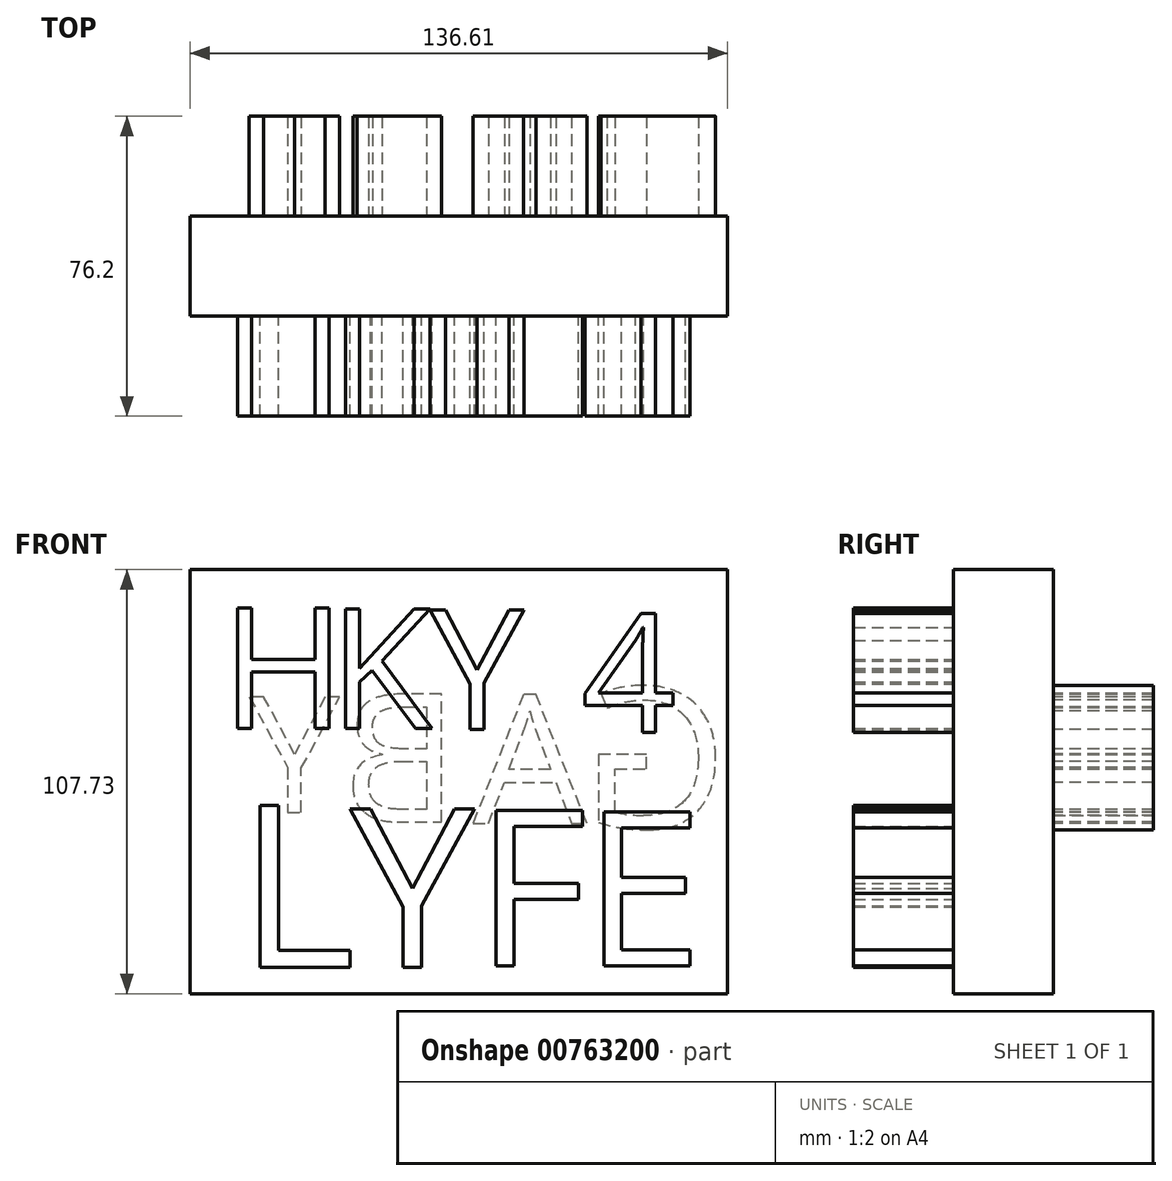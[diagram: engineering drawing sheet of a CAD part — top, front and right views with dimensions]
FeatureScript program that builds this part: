
annotation { "Feature Type Name" : "Feature", "Feature Type Description" : "" }
export const myFeature = defineFeature(function(context is Context, id is Id, definition is map)
    precondition{}
    {
        {
            var Q0;
            Q0=qCreatedBy(makeId("Front.planeOp"),FACE);
            var sketch = newSketch(context, id + "F0", { "sketchPlane" : qUnion([Q0])});
            skLineSegment(sketch, "E0.bottom", {"start": v(-70.77, 48.65) * mm, "end": v(65.84, 48.65) * mm});
            skLineSegment(sketch, "E0.top", {"start": v(-70.77, -59.08) * mm, "end": v(65.84, -59.08) * mm});
            skLineSegment(sketch, "E0.left", {"start": v(-70.77, 48.65) * mm, "end": v(-70.77, -59.08) * mm});
            skLineSegment(sketch, "E0.right", {"start": v(65.84, 48.65) * mm, "end": v(65.84, -59.08) * mm});
            skSolve(sketch);
        }
        {
            var Q0;
            Q0=makeQuery(id+"F0.imprint","IMPRINT",FACE,{"disambiguationData":[TD([[makeQuery(id+"F0.imprint","IMPRINT",EDGE,{"derivedFrom":sQuery(id+"F0.wireOp",EDGE,"E0.bottom")}),-1.0]])]});
            extrude(context, id + "F1", {"entities" : qUnion([Q0]), "depth" : 25.4 * mm, "offsetDistance" : 25.4 * mm});
        }
        {
            var Q0;
            Q0=makeQuery(id+"F1.opExtrude","CAP_FACE",FACE,{"disambiguationData":[OSD([sQuery(id+"F0.wireOp",EDGE,"E0.bottom"),sQuery(id+"F0.wireOp",EDGE,"E0.top"),sQuery(id+"F0.wireOp",EDGE,"E0.left"),sQuery(id+"F0.wireOp",EDGE,"E0.right")])],"isStart":false});
            var sketch = newSketch(context, id + "F2", { "sketchPlane" : qUnion([Q0])});
            skText(sketch, "E1", { "text": "H", "fontName": "OpenSans-Regular.ttf"});
            const initialGuessF2  = {"E1": [-0.06285, 0.00825, 1, 0, 0.0309]};
            skSetInitialGuess(sketch, initialGuessF2);
            skSolve(sketch);
        }
        {
            var Q0;
            Q0=makeQuery(id+"F2.imprint","IMPRINT",FACE,{"disambiguationData":[TD([[makeQuery(id+"F2.imprint","IMPRINT",EDGE,{"derivedFrom":sQuery(id+"F2.wireOp",EDGE,"E1.sketch_text.stroke-0")}),-1.0]])]});
            extrude(context, id + "F3", {"entities" : qUnion([Q0]), "operationType" : NewBodyOperationType.ADD, "depth" : 25.4 * mm, "offsetDistance" : 25.4 * mm});
        }
        {
            var Q0;
            Q0=makeQuery(id+"F1.opExtrude","CAP_FACE",FACE,{"disambiguationData":[OSD([sQuery(id+"F0.wireOp",EDGE,"E0.bottom"),sQuery(id+"F0.wireOp",EDGE,"E0.top"),sQuery(id+"F0.wireOp",EDGE,"E0.left"),sQuery(id+"F0.wireOp",EDGE,"E0.right")])],"isStart":false});
            var sketch = newSketch(context, id + "F4", { "sketchPlane" : qUnion([Q0])});
            skText(sketch, "E2", { "text": "K", "fontName": "OpenSans-Regular.ttf"});
            const initialGuessF4  = {"E2": [-0.03537, 0.00825, 1, 0, 0.03064]};
            skSetInitialGuess(sketch, initialGuessF4);
            skSolve(sketch);
        }
        {
            var Q0;
            Q0 = qSketchRegion(id + "F4", true);
            extrude(context, id + "F5", {"entities" : qUnion([Q0]), "operationType" : NewBodyOperationType.ADD, "depth" : 25.4 * mm, "offsetDistance" : 25.4 * mm});
        }
        {
            var Q0;
            Q0=makeQuery(id+"F1.opExtrude","CAP_FACE",FACE,{"disambiguationData":[OSD([sQuery(id+"F0.wireOp",EDGE,"E0.bottom"),sQuery(id+"F0.wireOp",EDGE,"E0.top"),sQuery(id+"F0.wireOp",EDGE,"E0.left"),sQuery(id+"F0.wireOp",EDGE,"E0.right")])],"isStart":false});
            var sketch = newSketch(context, id + "F6", { "sketchPlane" : qUnion([Q0])});
            skText(sketch, "E3", { "text": "Y", "fontName": "OpenSans-Regular.ttf"});
            const initialGuessF6  = {"E3": [-0.00971, 0.00806, 1, 0, 0.03057]};
            skSetInitialGuess(sketch, initialGuessF6);
            skSolve(sketch);
        }
        {
            var Q0;
            Q0 = qSketchRegion(id + "F6", true);
            extrude(context, id + "F7", {"entities" : qUnion([Q0]), "operationType" : NewBodyOperationType.ADD, "depth" : 25.4 * mm, "offsetDistance" : 25.4 * mm});
        }
        {
            var Q0;
            Q0=makeQuery(id+"F1.opExtrude","CAP_FACE",FACE,{"disambiguationData":[OSD([sQuery(id+"F0.wireOp",EDGE,"E0.bottom"),sQuery(id+"F0.wireOp",EDGE,"E0.top"),sQuery(id+"F0.wireOp",EDGE,"E0.left"),sQuery(id+"F0.wireOp",EDGE,"E0.right")])],"isStart":false});
            var sketch = newSketch(context, id + "F8", { "sketchPlane" : qUnion([Q0])});
            skText(sketch, "E4", { "text": "4", "fontName": "OpenSans-Regular.ttf"});
            const initialGuessF8  = {"E4": [0.02872, 0.0073, 1, 0, 0.03034]};
            skSetInitialGuess(sketch, initialGuessF8);
            skSolve(sketch);
        }
        {
            var Q0;
            Q0=makeQuery(id+"F8.imprint","IMPRINT",FACE,{"disambiguationData":[TD([[makeQuery(id+"F8.imprint","IMPRINT",EDGE,{"derivedFrom":sQuery(id+"F8.wireOp",EDGE,"E4.sketch_text.stroke-0")}),-1.0]])]});
            extrude(context, id + "F9", {"entities" : qUnion([Q0]), "operationType" : NewBodyOperationType.ADD, "depth" : 25.4 * mm, "offsetDistance" : 25.4 * mm});
        }
        {
            var Q0;
            {var subQ0=sQuery(id+"F0.wireOp",EDGE,"E0.top");var subQ1=sQuery(id+"F0.wireOp",EDGE,"E0.bottom");var subQ2=sQuery(id+"F0.wireOp",EDGE,"E0.left");var subQ3=sQuery(id+"F0.wireOp",EDGE,"E0.right");Q0=makeQuery(id+"F9.boolean.opBoolean","SPLIT",FACE,{"disambiguationData":[TD([makeQuery(id+"F1.opExtrude","SWEPT_FACE",FACE,{"disambiguationData":[OSD([subQ1])]})])],"derivedFrom":makeQuery(id+"F1.opExtrude","CAP_FACE",FACE,{"disambiguationData":[OSD([subQ1,subQ0,subQ2,subQ3])],"isStart":false})});}
            var sketch = newSketch(context, id + "F10", { "sketchPlane" : qUnion([Q0])});
            skText(sketch, "E5", { "text": "L", "fontName": "OpenSans-Regular.ttf"});
            const initialGuessF10  = {"E5": [-0.05864, -0.05242, 1, 0, 0.04152]};
            skSetInitialGuess(sketch, initialGuessF10);
            skSolve(sketch);
        }
        {
            var Q0;
            Q0 = qSketchRegion(id + "F10", true);
            extrude(context, id + "F11", {"entities" : qUnion([Q0]), "operationType" : NewBodyOperationType.ADD, "depth" : 25.4 * mm, "offsetDistance" : 25.4 * mm});
        }
        {
            var Q0;
            {var subQ0=sQuery(id+"F0.wireOp",EDGE,"E0.top");var subQ1=sQuery(id+"F0.wireOp",EDGE,"E0.bottom");var subQ2=sQuery(id+"F0.wireOp",EDGE,"E0.left");var subQ3=sQuery(id+"F0.wireOp",EDGE,"E0.right");Q0=makeQuery(id+"F9.boolean.opBoolean","SPLIT",FACE,{"disambiguationData":[TD([makeQuery(id+"F1.opExtrude","SWEPT_FACE",FACE,{"disambiguationData":[OSD([subQ1])]})])],"derivedFrom":makeQuery(id+"F1.opExtrude","CAP_FACE",FACE,{"disambiguationData":[OSD([subQ1,subQ0,subQ2,subQ3])],"isStart":false})});}
            var sketch = newSketch(context, id + "F12", { "sketchPlane" : qUnion([Q0])});
            skText(sketch, "E6", { "text": "Y", "fontName": "OpenSans-Regular.ttf"});
            const initialGuessF12  = {"E6": [-0.03003, -0.05242, 1, 0, 0.04057]};
            skSetInitialGuess(sketch, initialGuessF12);
            skSolve(sketch);
        }
        {
            var Q0;
            Q0=makeQuery(id+"F12.imprint","IMPRINT",FACE,{"disambiguationData":[TD([[makeQuery(id+"F12.imprint","IMPRINT",EDGE,{"derivedFrom":sQuery(id+"F12.wireOp",EDGE,"E6.sketch_text.stroke-0")}),-1.0]])]});
            extrude(context, id + "F13", {"entities" : qUnion([Q0]), "operationType" : NewBodyOperationType.ADD, "depth" : 25.4 * mm, "offsetDistance" : 25.4 * mm});
        }
        {
            var Q0;
            {var subQ0=sQuery(id+"F0.wireOp",EDGE,"E0.top");var subQ1=sQuery(id+"F0.wireOp",EDGE,"E0.bottom");var subQ2=sQuery(id+"F0.wireOp",EDGE,"E0.left");var subQ3=sQuery(id+"F0.wireOp",EDGE,"E0.right");Q0=makeQuery(id+"F9.boolean.opBoolean","SPLIT",FACE,{"disambiguationData":[TD([makeQuery(id+"F1.opExtrude","SWEPT_FACE",FACE,{"disambiguationData":[OSD([subQ1])]})])],"derivedFrom":makeQuery(id+"F1.opExtrude","CAP_FACE",FACE,{"disambiguationData":[OSD([subQ1,subQ0,subQ2,subQ3])],"isStart":false})});}
            var sketch = newSketch(context, id + "F14", { "sketchPlane" : qUnion([Q0])});
            skText(sketch, "E7", { "text": "F", "fontName": "OpenSans-Regular.ttf"});
            const initialGuessF14  = {"E7": [0.00153, -0.05204, 1, 0, 0.03985]};
            skSetInitialGuess(sketch, initialGuessF14);
            skSolve(sketch);
        }
        {
            var Q0;
            Q0=makeQuery(id+"F14.imprint","IMPRINT",FACE,{"disambiguationData":[TD([[makeQuery(id+"F14.imprint","IMPRINT",EDGE,{"derivedFrom":sQuery(id+"F14.wireOp",EDGE,"E7.sketch_text.stroke-0")}),-1.0]])]});
            extrude(context, id + "F15", {"entities" : qUnion([Q0]), "operationType" : NewBodyOperationType.ADD, "depth" : 25.4 * mm, "offsetDistance" : 25.4 * mm});
        }
        {
            var Q0;
            {var subQ0=sQuery(id+"F0.wireOp",EDGE,"E0.top");var subQ1=sQuery(id+"F0.wireOp",EDGE,"E0.bottom");var subQ2=sQuery(id+"F0.wireOp",EDGE,"E0.left");var subQ3=sQuery(id+"F0.wireOp",EDGE,"E0.right");Q0=makeQuery(id+"F9.boolean.opBoolean","SPLIT",FACE,{"disambiguationData":[TD([makeQuery(id+"F1.opExtrude","SWEPT_FACE",FACE,{"disambiguationData":[OSD([subQ1])]})])],"derivedFrom":makeQuery(id+"F1.opExtrude","CAP_FACE",FACE,{"disambiguationData":[OSD([subQ1,subQ0,subQ2,subQ3])],"isStart":false})});}
            var sketch = newSketch(context, id + "F16", { "sketchPlane" : qUnion([Q0])});
            skText(sketch, "E8", { "text": "E", "fontName": "OpenSans-Regular.ttf"});
            const initialGuessF16  = {"E8": [0.02899, -0.05204, 1, 0, 0.03951]};
            skSetInitialGuess(sketch, initialGuessF16);
            skSolve(sketch);
        }
        {
            var Q0;
            Q0=makeQuery(id+"F16.imprint","IMPRINT",FACE,{"disambiguationData":[TD([[makeQuery(id+"F16.imprint","IMPRINT",EDGE,{"derivedFrom":sQuery(id+"F16.wireOp",EDGE,"E8.sketch_text.stroke-0")}),-1.0]])]});
            extrude(context, id + "F17", {"entities" : qUnion([Q0]), "operationType" : NewBodyOperationType.ADD, "depth" : 25.4 * mm, "offsetDistance" : 25.4 * mm});
        }
        {
            var Q0;
            Q0=makeQuery(id+"F1.opExtrude","CAP_FACE",FACE,{"disambiguationData":[OSD([sQuery(id+"F0.wireOp",EDGE,"E0.bottom"),sQuery(id+"F0.wireOp",EDGE,"E0.top"),sQuery(id+"F0.wireOp",EDGE,"E0.left"),sQuery(id+"F0.wireOp",EDGE,"E0.right")])],"isStart":true});
            var sketch = newSketch(context, id + "F18", { "sketchPlane" : qUnion([Q0])});
            skText(sketch, "E9", { "text": "G", "fontName": "OpenSans-Regular.ttf"});
            const initialGuessF18  = {"E9": [-0.06584, -0.01696, 1, 0, 0.03601]};
            skSetInitialGuess(sketch, initialGuessF18);
            skSolve(sketch);
        }
        {
            var Q0;
            Q0=makeQuery(id+"F18.imprint","IMPRINT",FACE,{"disambiguationData":[TD([[makeQuery(id+"F18.imprint","IMPRINT",EDGE,{"derivedFrom":sQuery(id+"F18.wireOp",EDGE,"E9.sketch_text.stroke-0")}),-1.0]])]});
            extrude(context, id + "F19", {"entities" : qUnion([Q0]), "operationType" : NewBodyOperationType.ADD, "depth" : 25.4 * mm, "offsetDistance" : 25.4 * mm});
        }
        {
            var Q0;
            Q0=makeQuery(id+"F1.opExtrude","CAP_FACE",FACE,{"disambiguationData":[OSD([sQuery(id+"F0.wireOp",EDGE,"E0.bottom"),sQuery(id+"F0.wireOp",EDGE,"E0.top"),sQuery(id+"F0.wireOp",EDGE,"E0.left"),sQuery(id+"F0.wireOp",EDGE,"E0.right")])],"isStart":true});
            var sketch = newSketch(context, id + "F20", { "sketchPlane" : qUnion([Q0])});
            skText(sketch, "E10", { "text": "A", "fontName": "OpenSans-Regular.ttf"});
            const initialGuessF20  = {"E10": [-0.03005, -0.01583, 1, 0, 0.03288]};
            skSetInitialGuess(sketch, initialGuessF20);
            skSolve(sketch);
        }
        {
            var Q0;
            Q0=makeQuery(id+"F20.imprint","IMPRINT",FACE,{"disambiguationData":[TD([[makeQuery(id+"F20.imprint","IMPRINT",EDGE,{"derivedFrom":sQuery(id+"F20.wireOp",EDGE,"E10.sketch_text.stroke-0")}),-1.0]])]});
            extrude(context, id + "F21", {"entities" : qUnion([Q0]), "operationType" : NewBodyOperationType.ADD, "depth" : 25.4 * mm, "offsetDistance" : 25.4 * mm});
        }
        {
            var Q0;
            {var subQ0=sQuery(id+"F0.wireOp",EDGE,"E0.bottom");var subQ1=sQuery(id+"F0.wireOp",EDGE,"E0.left");var subQ2=sQuery(id+"F0.wireOp",EDGE,"E0.top");var subQ3=sQuery(id+"F0.wireOp",EDGE,"E0.right");Q0=makeQuery(id+"F21.boolean.opBoolean","SPLIT",FACE,{"disambiguationData":[TD([makeQuery(id+"F1.opExtrude","SWEPT_FACE",FACE,{"disambiguationData":[OSD([subQ0])]})])],"derivedFrom":makeQuery(id+"F1.opExtrude","CAP_FACE",FACE,{"disambiguationData":[OSD([subQ0,subQ2,subQ1,subQ3])],"isStart":true})});}
            var sketch = newSketch(context, id + "F22", { "sketchPlane" : qUnion([Q0])});
            skText(sketch, "E11", { "text": "B", "fontName": "OpenSans-Regular.ttf"});
            const initialGuessF22  = {"E11": [0.00237, -0.01545, 1, 0, 0.0328]};
            skSetInitialGuess(sketch, initialGuessF22);
            skSolve(sketch);
        }
        {
            var Q0;
            Q0=makeQuery(id+"F22.imprint","IMPRINT",FACE,{"disambiguationData":[TD([[makeQuery(id+"F22.imprint","IMPRINT",EDGE,{"derivedFrom":sQuery(id+"F22.wireOp",EDGE,"E11.sketch_text.stroke-0")}),-1.0]])]});
            extrude(context, id + "F23", {"entities" : qUnion([Q0]), "operationType" : NewBodyOperationType.ADD, "depth" : 25.4 * mm, "offsetDistance" : 25.4 * mm});
        }
        {
            var Q0;
            {var subQ2=sQuery(id+"F0.wireOp",EDGE,"E0.bottom");var subQ3=makeQuery(id+"F1.opExtrude","SWEPT_FACE",FACE,{"disambiguationData":[OSD([subQ2])]});var subQ17=sQuery(id+"F0.wireOp",EDGE,"E0.left");var subQ21=sQuery(id+"F0.wireOp",EDGE,"E0.top");var subQ28=sQuery(id+"F0.wireOp",EDGE,"E0.right");Q0=makeQuery(id+"F23.boolean.opBoolean","SPLIT",FACE,{"disambiguationData":[TD([subQ3])],"derivedFrom":makeQuery(id+"F21.boolean.opBoolean","SPLIT",FACE,{"disambiguationData":[TD([subQ3])],"derivedFrom":makeQuery(id+"F1.opExtrude","CAP_FACE",FACE,{"disambiguationData":[OSD([subQ2,subQ21,subQ17,subQ28])],"isStart":true})})});}
            var sketch = newSketch(context, id + "F24", { "sketchPlane" : qUnion([Q0])});
            skText(sketch, "E12", { "text": "Y", "fontName": "OpenSans-Regular.ttf"});
            const initialGuessF24  = {"E12": [0.0327, -0.01299, 1, 0, 0.02958]};
            skSetInitialGuess(sketch, initialGuessF24);
            skSolve(sketch);
        }
        {
            var Q0;
            Q0 = qSketchRegion(id + "F24", true);
            extrude(context, id + "F25", {"entities" : qUnion([Q0]), "operationType" : NewBodyOperationType.ADD, "depth" : 25.4 * mm, "offsetDistance" : 25.4 * mm});
        }
    });
